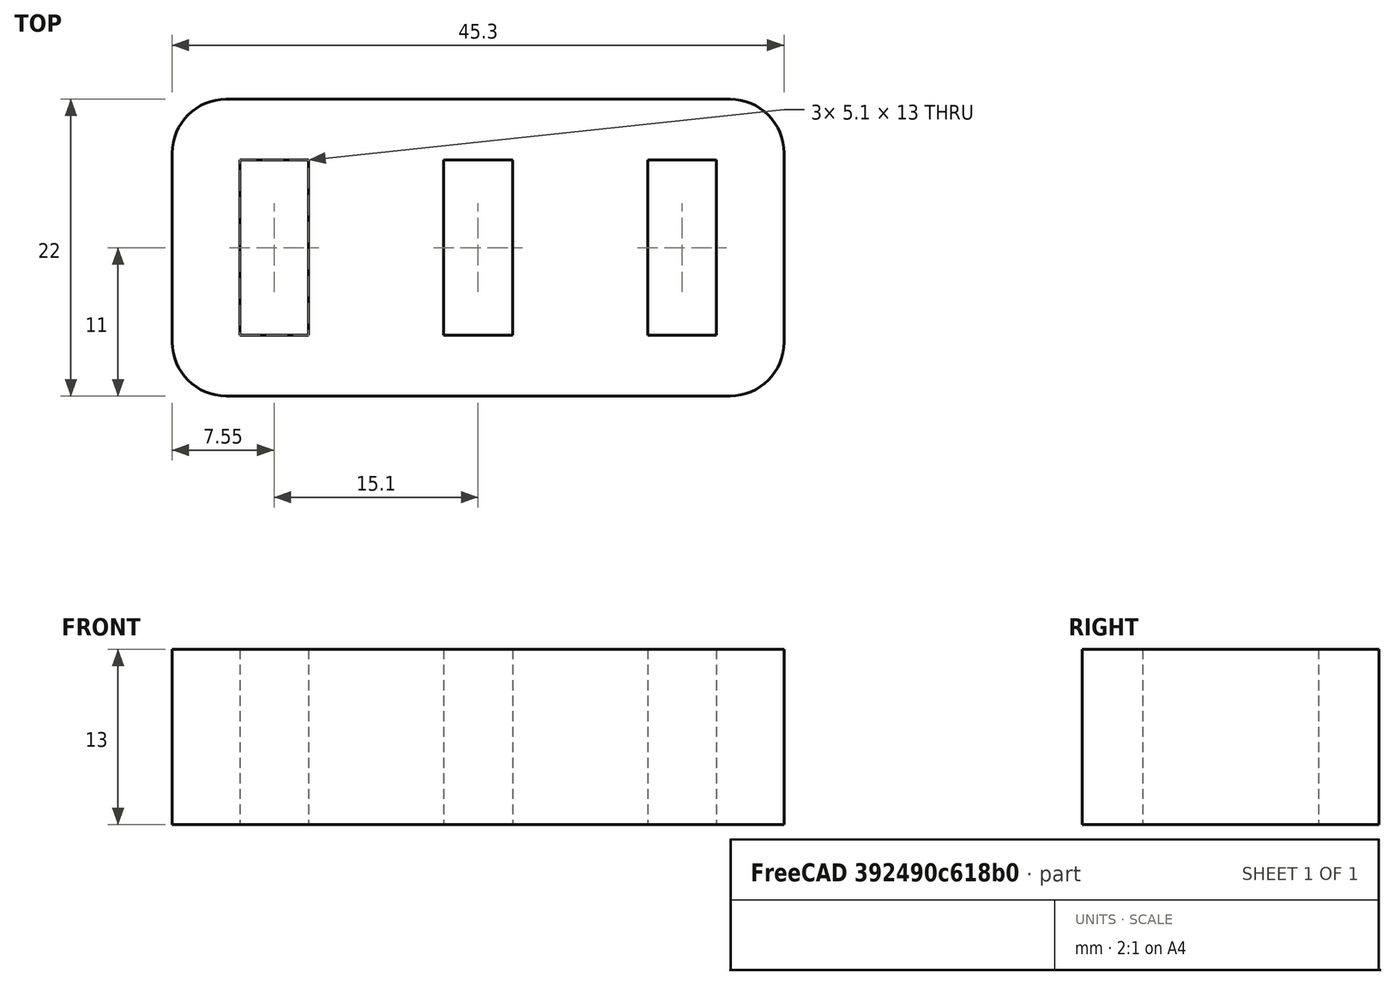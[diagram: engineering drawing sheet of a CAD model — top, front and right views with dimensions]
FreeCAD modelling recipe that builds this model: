
FCSTD DOCUMENT  (FreeCAD 0.17R13217 (Git))
Label: 02-1-porta-pendrive
License: All rights reserved
LicenseURL: http://en.wikipedia.org/wiki/All_rights_reserved
objects: TechDraw::DrawViewDimension×8, TechDraw::DrawProjGroupItem×2, Sketcher::SketchObject×1, PartDesign::Pad×1, PartDesign::Fillet×1, PartDesign::Body×1, TechDraw::DrawSVGTemplate×1, TechDraw::DrawProjGroup×1, TechDraw::DrawViewPart×1, TechDraw::DrawViewAnnotation×1, TechDraw::DrawPage×1
note: 5 computed .brp shape members not serialized (recipe doc carries the construction recipe); baked Part::Feature solids carry a one-line shape summary decoded from their .brp

FEATURE [Sketcher::SketchObject] Sketch
  MapMode = 5
  Support = -> [XY_Plane]
  sketch-geometry (16):
    g0: LineSegment StartX=-22.65 StartY=11 StartZ=0 EndX=22.65 EndY=11 EndZ=0
    g1: LineSegment StartX=22.65 StartY=11 StartZ=0 EndX=22.65 EndY=-11 EndZ=0
    g2: LineSegment StartX=22.65 StartY=-11 StartZ=0 EndX=-22.65 EndY=-11 EndZ=0
    g3: LineSegment StartX=-22.65 StartY=-11 StartZ=0 EndX=-22.65 EndY=11 EndZ=0
    g4: LineSegment StartX=-2.55 StartY=6.5 StartZ=0 EndX=2.55 EndY=6.5 EndZ=0
    g5: LineSegment StartX=2.55 StartY=6.5 StartZ=0 EndX=2.55 EndY=-6.5 EndZ=0
    g6: LineSegment StartX=2.55 StartY=-6.5 StartZ=0 EndX=-2.55 EndY=-6.5 EndZ=0
    g7: LineSegment StartX=-2.55 StartY=-6.5 StartZ=0 EndX=-2.55 EndY=6.5 EndZ=0
    g8: LineSegment StartX=-17.65 StartY=6.5 StartZ=0 EndX=-12.55 EndY=6.5 EndZ=0
    g9: LineSegment StartX=-12.55 StartY=6.5 StartZ=0 EndX=-12.55 EndY=-6.5 EndZ=0
    g10: LineSegment StartX=-12.55 StartY=-6.5 StartZ=0 EndX=-17.65 EndY=-6.5 EndZ=0
    g11: LineSegment StartX=-17.65 StartY=-6.5 StartZ=0 EndX=-17.65 EndY=6.5 EndZ=0
    g12: LineSegment StartX=12.55 StartY=6.5 StartZ=0 EndX=17.65 EndY=6.5 EndZ=0
    g13: LineSegment StartX=17.65 StartY=6.5 StartZ=0 EndX=17.65 EndY=-6.5 EndZ=0
    g14: LineSegment StartX=17.65 StartY=-6.5 StartZ=0 EndX=12.55 EndY=-6.5 EndZ=0
    g15: LineSegment StartX=12.55 StartY=-6.5 StartZ=0 EndX=12.55 EndY=6.5 EndZ=0
  constraints (44):
    c: Coincident(g0,g1)
    c: Coincident(g1,g2)
    c: Coincident(g2,g3)
    c: Coincident(g3,g0)
    c: Horizontal(g0)
    c: Horizontal(g2)
    c: Vertical(g1)
    c: Vertical(g3)
    c: Symmetric(g0,g1,g-1)
    c: Coincident(g4,g5)
    c: Coincident(g5,g6)
    c: Coincident(g6,g7)
    c: Coincident(g7,g4)
    c: Horizontal(g4)
    c: Horizontal(g6)
    c: Vertical(g5)
    c: Vertical(g7)
    c: Symmetric(g4,g5,g-1)
    c: Coincident(g8,g9)
    c: Coincident(g9,g10)
    c: Coincident(g10,g11)
    c: Coincident(g11,g8)
    c: Horizontal(g8)
    c: Horizontal(g10)
    c: Vertical(g9)
    c: Vertical(g11)
    c: Coincident(g12,g13)
    c: Coincident(g13,g14)
    c: Coincident(g14,g15)
    c: Coincident(g15,g12)
    c: Horizontal(g12)
    c: Horizontal(g14)
    c: Vertical(g13)
    c: Vertical(g15)
    c: PointOnObject(g9,g6)
    c: PointOnObject(g8,g4)
    c: Symmetric(g8,g12,g-2)
    c: Symmetric(g14,g9,g-2)
    c: Equal(g4,g8)
    c: DistanceX(g4,g4) = 5.1
    c: DistanceX(g8,g4) = 10
    c: DistanceX(g0,g8) = 5
    c: DistanceY(g3,g3) = 22
    c: DistanceY(g5,g5) = 13
FEATURE [PartDesign::Pad] Pad  label="Cuerpo-ranuras"
  Length = 13
  Length2 = 100
  Profile = -> Sketch
  Refine = true
  Reversed = true
  Type = 0
FEATURE [PartDesign::Fillet] Fillet  label="redonde-esquinas"
  Base = -> Pad [Edge8,Edge5,Edge2,Edge1]
  BaseFeature = -> Pad
  Radius = 4
FEATURE [PartDesign::Body] Body  label="Porta-pendrive"
  Group = -> [Sketch,Pad,Fillet]
  Origin = -> Origin
  Tip = -> Fillet
FEATURE [TechDraw::DrawSVGTemplate] Template
  EditableTexts = Designed_by_Name=Designed by Name; Drawing_number=Drawing number; FC-Date=Date; FC-SC=Scale; FC-SH=Sheet; FC-Title=Title; Subtitle=Subtitle; Weight=Weight
  Height = 210
  Orientation = 1
  Width = 297
FEATURE [TechDraw::DrawProjGroupItem] ProjItem  label="Front"
  ArcCenterMarks = true
  CenterScale = 2
  CoarseView = false
  Direction = (0,-1,0)
  ExtraWidth = 1.4
  Focus = 100
  HardHidden = true
  HiddenWidth = 0.35
  HorizCenterLine = false
  IsoCount = 0
  IsoHidden = true
  IsoVisible = true
  IsoWidth = 0.5
  KeepLabel = false
  LineWidth = 0.7
  LockPosition = false
  Perspective = false
  Rotation = 0
  RotationVector = (1,0,0)
  ScaleType = 0
  SeamHidden = false
  SeamVisible = true
  ShowSectionLine = true
  SmoothHidden = false
  SmoothVisible = false
  Source = -> [Fillet]
  Type = 0
  VertCenterLine = false
  X = 0
  Y = -20.75
FEATURE [TechDraw::DrawProjGroupItem] ProjItem001  label="Bottom"
  ArcCenterMarks = true
  CenterScale = 2
  CoarseView = false
  Direction = (0,0,-1)
  ExtraWidth = 1.4
  Focus = 100
  HardHidden = true
  HiddenWidth = 0.35
  HorizCenterLine = false
  IsoCount = 0
  IsoHidden = false
  IsoVisible = false
  IsoWidth = 0.5
  KeepLabel = false
  LineWidth = 0.7
  LockPosition = false
  Perspective = false
  Rotation = 0
  RotationVector = (1,0,0)
  ScaleType = 0
  SeamHidden = false
  SeamVisible = false
  ShowSectionLine = true
  SmoothHidden = false
  SmoothVisible = false
  Source = -> [Fillet]
  Type = 5
  VertCenterLine = false
  X = 0
  Y = 62
FEATURE [TechDraw::DrawProjGroup] ProjGroup
  Anchor = -> ProjItem
  AutoDistribute = true
  CubeDirs = (1) [(0,0,0)]
  CubeRotations = (1) [(0,0,0)]
  KeepLabel = false
  LockPosition = false
  ProjectionType = 0
  Rotation = 0
  ScaleType = 0
  Source = -> [Fillet]
  Views = -> [ProjItem,ProjItem001]
  X = 88.3592
  Y = 73.6972
  spacingX = 15
  spacingY = 40
FEATURE [TechDraw::DrawViewPart] View
  ArcCenterMarks = true
  CenterScale = 2
  CoarseView = false
  Direction = (1,1,1)
  ExtraWidth = 1.4
  Focus = 100
  HardHidden = true
  HiddenWidth = 0.35
  HorizCenterLine = false
  IsoCount = 0
  IsoHidden = false
  IsoVisible = false
  IsoWidth = 0.5
  KeepLabel = false
  LineWidth = 0.7
  LockPosition = false
  Perspective = false
  Rotation = 0
  ScaleType = 0
  SeamHidden = false
  SeamVisible = false
  ShowSectionLine = true
  SmoothHidden = false
  SmoothVisible = false
  Source = -> [Fillet]
  VertCenterLine = false
  X = 212.092
  Y = 111.901
FEATURE [TechDraw::DrawViewDimension] Dimension
  Font = osifont
  Fontsize = 3.5
  FormatSpec = %.2f
  KeepLabel = false
  LineWidth = 0.5
  LockPosition = false
  MeasureType = 1
  References2D = -> [ProjItem]
  Rotation = 0
  ScaleType = 0
  Type = 2
  X = 29.5775
  Y = 23.169
FEATURE [TechDraw::DrawViewDimension] Dimension002
  Font = osifont
  Fontsize = 3.5
  FormatSpec = %.2f
  KeepLabel = false
  LineWidth = 0.5
  LockPosition = false
  MeasureType = 1
  References2D = -> [ProjItem]
  Rotation = 0
  ScaleType = 0
  Type = 1
  X = -3.20423
  Y = 23.4155
FEATURE [TechDraw::DrawViewDimension] Dimension003
  Font = osifont
  Fontsize = 3.5
  FormatSpec = %.2f
  KeepLabel = false
  LineWidth = 0.5
  LockPosition = false
  MeasureType = 1
  References2D = -> [ProjItem001]
  Rotation = 0
  ScaleType = 0
  Type = 2
  X = -49.2958
  Y = -30.8099
FEATURE [TechDraw::DrawViewDimension] Dimension004
  Font = osifont
  Fontsize = 3.5
  FormatSpec = %.2f
  KeepLabel = false
  LineWidth = 0.5
  LockPosition = false
  MeasureType = 1
  References2D = -> [ProjItem001]
  Rotation = 0
  ScaleType = 0
  Type = 2
  X = 35.493
  Y = -21.6901
FEATURE [TechDraw::DrawViewDimension] Dimension005
  Font = osifont
  Fontsize = 3.5
  FormatSpec = %.2f
  KeepLabel = false
  LineWidth = 0.5
  LockPosition = false
  MeasureType = 1
  References2D = -> [ProjItem001]
  Rotation = 0
  ScaleType = 0
  Type = 1
  X = 19.9648
  Y = -25.8803
FEATURE [TechDraw::DrawViewDimension] Dimension006
  Font = osifont
  Fontsize = 3.5
  FormatSpec = %.2f
  KeepLabel = false
  LineWidth = 0.5
  LockPosition = false
  MeasureType = 1
  References2D = -> [ProjItem001]
  Rotation = 0
  ScaleType = 0
  Type = 4
  X = -49.7887
  Y = 27.6056
FEATURE [TechDraw::DrawViewAnnotation] Annotation
  Font = osifont
  KeepLabel = false
  LineSpace = 80
  LockPosition = false
  MaxWidth = -1
  Rotation = 0
  ScaleType = 0
  Text = Portapendrives
  TextSize = 8
  TextStyle = 0
  X = 208.887
  Y = 162.183
FEATURE [TechDraw::DrawViewDimension] Dimension007
  Font = osifont
  Fontsize = 3.5
  FormatSpec = %.2f
  KeepLabel = false
  LineWidth = 0.5
  LockPosition = false
  MeasureType = 1
  References2D = -> [ProjItem001]
  Rotation = 0
  ScaleType = 0
  Type = 1
  X = 16.6503
  Y = 23.6254
FEATURE [TechDraw::DrawViewDimension] Dimension008
  Font = osifont
  Fontsize = 3.5
  FormatSpec = %.2f
  KeepLabel = false
  LineWidth = 0.5
  LockPosition = false
  MeasureType = 1
  References2D = -> [ProjItem001]
  Rotation = 0
  ScaleType = 0
  Type = 1
  X = 7.87512
  Y = -33.9755
FEATURE [TechDraw::DrawPage] Page  label="planos"
  KeepUpdated = true
  ProjectionType = 0
  Template = -> Template
  Views = -> [ProjGroup,View,Dimension,Dimension002,Dimension003,Dimension004,Dimension005,Dimension006,Annotation,Dimension007,Dimension008]
